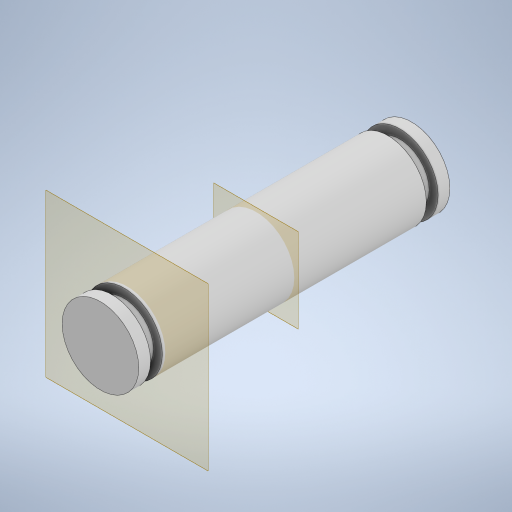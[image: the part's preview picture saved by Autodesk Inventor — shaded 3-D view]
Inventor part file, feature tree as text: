
AUTODESK INVENTOR PART (.ipt)
format: ipt  version: 2024 (Build 280153000, 153)  size: 617,472 bytes
history: native  units: mm
features: plane x3, sketch x3, extrude x3, other x3, move_body x2, direct_edit x1, mirror x1, reference x1, projected_geometry x1
ambient origin geometry x8: Origin, YZ Plane, XZ Plane, XY Plane, X Axis, Y Axis, Z Axis, Center Point
bodies: Solid1 (feature_tree)
feature tree (18):
  plane  "Work Plane1"
  sketch  "Sketch1"  dims[d0=0.5mm d1=10.0mm d2=0.0mm]
  plane  "Work Plane2"
  extrude  "Extrusion1"  Depth=10.0mm TaperAngle=0.0deg
  direct_edit  "Direct Edit1"
  extrude  "Extrusion3"  Depth=1.0mm TaperAngle=0.0deg
  extrude  "Extrusion4"  Depth=4.0mm TaperAngle=0.0deg
  plane  "Work Plane3"
  mirror  "Mirror1"
  reference  "Reference1"
  sketch  "Sketch3"  dims[d5=0.0mm d6=0.0mm d7=1.0mm d8=0.0mm d9=0.0mm d10=1.0mm]
  sketch  "Sketch4"  dims[d11=20.0mm d12=4.0mm d13=0.0mm d14=4.0mm d15=0.0mm]
  projected_geometry  "Projected Loop2"
  other  "<userpath>\Documents\Inventor\robot arm\arms\arms.iam"
  other  "arms.iam"
  other  "middle arm pulley:2"
  move_body  "Move1"
  move_body  "Move2"
